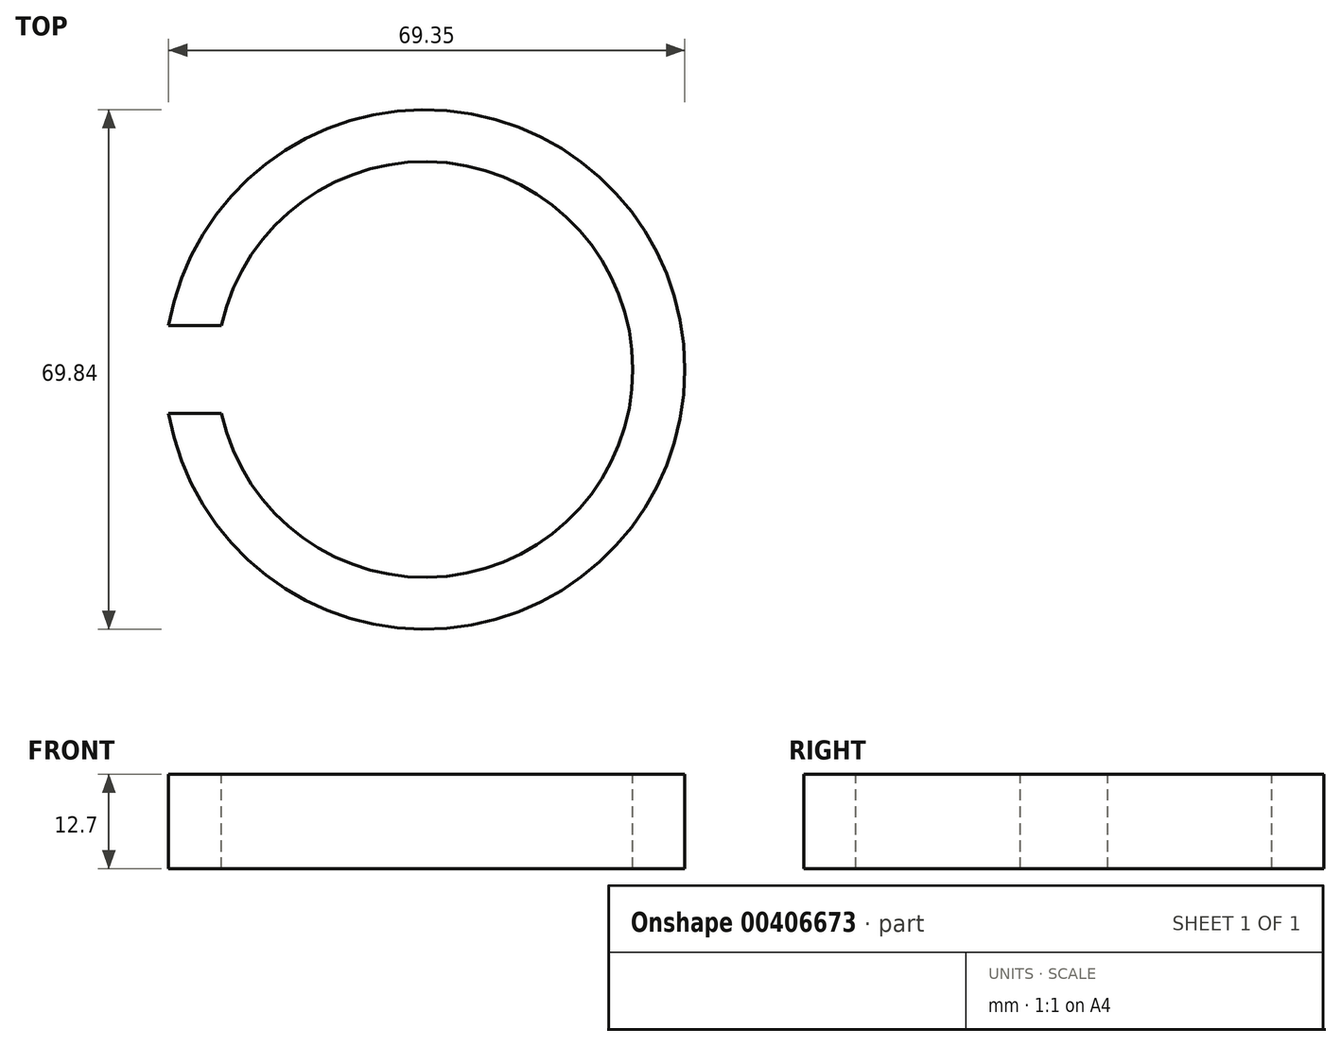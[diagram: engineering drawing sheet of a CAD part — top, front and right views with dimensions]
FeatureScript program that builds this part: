
annotation { "Feature Type Name" : "Feature", "Feature Type Description" : "" }
export const myFeature = defineFeature(function(context is Context, id is Id, definition is map)
    precondition{}
    {
        {
            var Q0;
            Q0=qCreatedBy(makeId("Top.planeOp"),FACE);
            var sketch = newSketch(context, id + "F0", { "sketchPlane" : qUnion([Q0])});
            skLineSegment(sketch, "E0", {"start": v(-34.43, -5.88) * mm, "end": v(-27.32, -5.88) * mm});
            skLineSegment(sketch, "E1", {"start": v(-27.32, 5.88) * mm, "end": v(-34.43, 5.88) * mm});
            skArc(sketch, "E2", {"start": v(-27.32, -5.88) * mm, "mid": v(27.94, 0) * mm, "end": v(-27.32, 5.88) * mm});
            skArc(sketch, "E3", {"start": v(-34.43, -5.88) * mm, "mid": v(34.93, 0) * mm, "end": v(-34.43, 5.88) * mm});
            skSolve(sketch);
        }
        {
            var Q0;
            Q0 = qSketchRegion(id + "F0", true);
            extrude(context, id + "F1", {"entities" : qUnion([Q0]), "oppositeDirection" : true, "depth" : 12.7 * mm});
        }
    });
